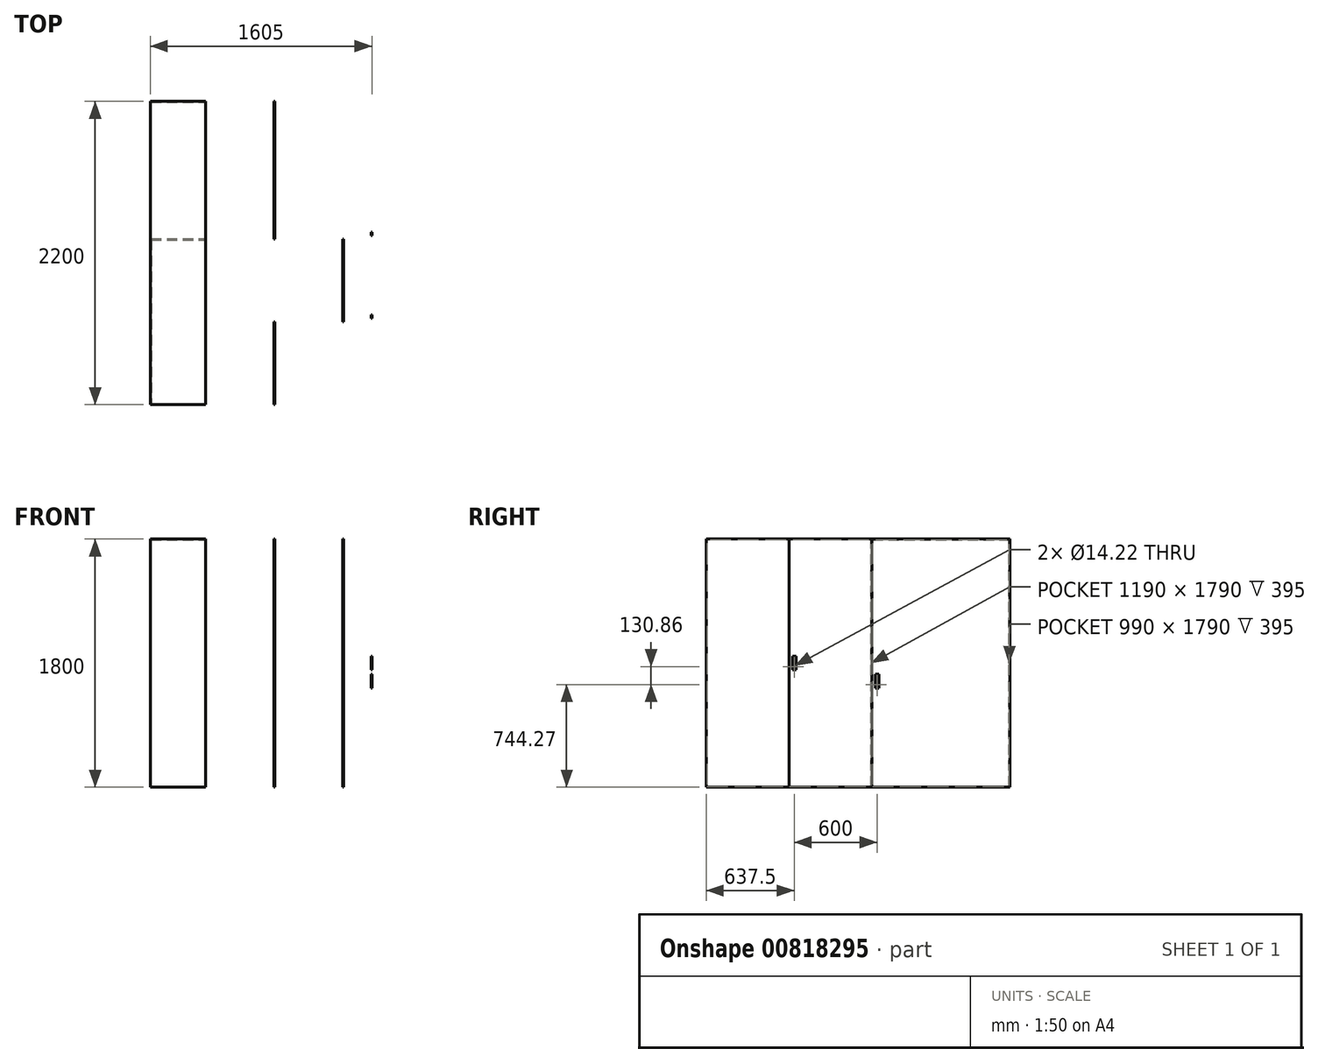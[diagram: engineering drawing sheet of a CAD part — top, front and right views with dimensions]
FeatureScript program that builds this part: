
annotation { "Feature Type Name" : "Feature", "Feature Type Description" : "" }
export const myFeature = defineFeature(function(context is Context, id is Id, definition is map)
    precondition{}
    {
        {
            var Q0;
            Q0=qCreatedBy(makeId("Right.planeOp"),FACE);
            var sketch = newSketch(context, id + "F0", { "sketchPlane" : qUnion([Q0])});
            skLineSegment(sketch, "E0.bottom", {"start": v(0, 0) * mm, "end": v(-1200, 0) * mm});
            skLineSegment(sketch, "E0.top", {"start": v(0, 1800) * mm, "end": v(-1200, 1800) * mm});
            skLineSegment(sketch, "E0.left", {"start": v(0, 0) * mm, "end": v(0, 1800) * mm});
            skLineSegment(sketch, "E0.right", {"start": v(-1200, 0) * mm, "end": v(-1200, 1800) * mm});
            skSolve(sketch);
        }
        {
            var Q0;
            Q0 = qSketchRegion(id + "F0", true);
            extrude(context, id + "F1", {"entities" : qUnion([Q0]), "oppositeDirection" : true, "depth" : 400 * mm, "offsetDistance" : 25 * mm});
        }
        {
            var Q0;
            Q0=qCreatedBy(makeId("Right.planeOp"),FACE);
            var sketch = newSketch(context, id + "F2", { "sketchPlane" : qUnion([Q0])});
            skLineSegment(sketch, "E1.bottom", {"start": v(0, 0) * mm, "end": v(1000, 0) * mm});
            skLineSegment(sketch, "E1.top", {"start": v(0, 1800) * mm, "end": v(1000, 1800) * mm});
            skLineSegment(sketch, "E1.left", {"start": v(0, 0) * mm, "end": v(0, 1800) * mm});
            skLineSegment(sketch, "E1.right", {"start": v(1000, 0) * mm, "end": v(1000, 1800) * mm});
            skSolve(sketch);
        }
        {
            var Q0;
            Q0 = qSketchRegion(id + "F2", true);
            extrude(context, id + "F3", {"entities" : qUnion([Q0]), "oppositeDirection" : true, "depth" : 400 * mm, "offsetDistance" : 25 * mm});
        }
        {
            var Q0;
            Q0=makeQuery(id+"F1.opExtrude","CAP_FACE",FACE,{"disambiguationData":[OSD([sQuery(id+"F0.wireOp",EDGE,"E0.bottom"),sQuery(id+"F0.wireOp",EDGE,"E0.top"),sQuery(id+"F0.wireOp",EDGE,"E0.right"),sQuery(id+"F0.wireOp",EDGE,"E0.left")])],"isStart":true});
            var Q1;
            Q1=makeQuery(id+"F3.opExtrude","CAP_FACE",FACE,{"disambiguationData":[OSD([sQuery(id+"F2.wireOp",EDGE,"E1.bottom"),sQuery(id+"F2.wireOp",EDGE,"E1.top"),sQuery(id+"F2.wireOp",EDGE,"E1.left"),sQuery(id+"F2.wireOp",EDGE,"E1.right")])],"isStart":true});
            shell(context, id + "F4", {"entities" : qUnion([Q0, Q1]), "thickness" : 5 * mm});
        }
        {
            var Q0;
            Q0=makeQuery(id+"F1.opExtrude","SWEPT_BODY",BODY,{"disambiguationData":[OSD([sQuery(id+"F0.wireOp",EDGE,"E0.bottom"),sQuery(id+"F0.wireOp",EDGE,"E0.top"),sQuery(id+"F0.wireOp",EDGE,"E0.right"),sQuery(id+"F0.wireOp",EDGE,"E0.left")])]});
            var Q1;
            Q1=makeQuery(id+"F3.opExtrude","SWEPT_BODY",BODY,{"disambiguationData":[OSD([sQuery(id+"F2.wireOp",EDGE,"E1.bottom"),sQuery(id+"F2.wireOp",EDGE,"E1.top"),sQuery(id+"F2.wireOp",EDGE,"E1.left"),sQuery(id+"F2.wireOp",EDGE,"E1.right")])]});
            booleanBodies(context, id + "F5", {"operationType" : BooleanOperationType.UNION, "tools" : qUnion([Q0, Q1])});
        }
        {
            var Q0;
            Q0=qCreatedBy(makeId("Right.planeOp"),FACE);
            cPlane(context, id + "F6", {"entities" : qUnion([Q0]), "cplaneType" : CPlaneType.OFFSET, "offset" : 500 * mm, "width" : 150 * mm, "height" : 150 * mm});
        }
        {
            var Q0;
            Q0=qCreatedBy(id+"F6.planeOp",FACE);
            var sketch = newSketch(context, id + "F7", { "sketchPlane" : qUnion([Q0])});
            skLineSegment(sketch, "E2.0", {"start": v(1000, 0) * mm, "end": v(1000, 1800) * mm});
            skLineSegment(sketch, "E3.0", {"start": v(-1200, 0) * mm, "end": v(-1200, 1800) * mm});
            skLineSegment(sketch, "E4", {"start": v(1000, 0) * mm, "end": v(0, 0) * mm});
            skLineSegment(sketch, "E5", {"start": v(0, 0) * mm, "end": v(0, 1800) * mm});
            skLineSegment(sketch, "E6", {"start": v(0, 1800) * mm, "end": v(1000, 1800) * mm});
            skLineSegment(sketch, "E7", {"start": v(-1200, 1800) * mm, "end": v(-600, 1800) * mm});
            skLineSegment(sketch, "E8", {"start": v(-600, 1800) * mm, "end": v(-600, 0) * mm});
            skLineSegment(sketch, "E9", {"start": v(-600, 0) * mm, "end": v(-1200, 0) * mm});
            skSolve(sketch);
        }
        {
            var Q0;
            Q0 = qSketchRegion(id + "F7", true);
            extrude(context, id + "F8", {"entities" : qUnion([Q0]), "oppositeDirection" : true, "depth" : 5 * mm, "offsetDistance" : 25 * mm});
        }
        {
            var Q0;
            Q0=qCreatedBy(id+"F6.planeOp",FACE);
            cPlane(context, id + "F9", {"entities" : qUnion([Q0]), "cplaneType" : CPlaneType.OFFSET, "offset" : 500 * mm, "width" : 150 * mm, "height" : 150 * mm});
        }
        {
            var Q0;
            Q0=qCreatedBy(id+"F9.planeOp",FACE);
            var sketch = newSketch(context, id + "F10", { "sketchPlane" : qUnion([Q0])});
            skLineSegment(sketch, "E10.0", {"start": v(-600, 1800) * mm, "end": v(-600, 0) * mm});
            skLineSegment(sketch, "E11.0", {"start": v(0, 0) * mm, "end": v(0, 1800) * mm});
            skLineSegment(sketch, "E12", {"start": v(-600, 1800) * mm, "end": v(0, 1800) * mm});
            skLineSegment(sketch, "E13", {"start": v(-600, 0) * mm, "end": v(0, 0) * mm});
            skSolve(sketch);
        }
        {
            var Q0;
            Q0 = qSketchRegion(id + "F10", true);
            extrude(context, id + "F11", {"entities" : qUnion([Q0]), "oppositeDirection" : true, "depth" : 5 * mm, "offsetDistance" : 25 * mm});
        }
        {
            var Q0;
            Q0=makeQuery(id+"F11.opExtrude","CAP_FACE",FACE,{"disambiguationData":[OSD([sQuery(id+"F10.wireOp",EDGE,"E10.0"),sQuery(id+"F10.wireOp",EDGE,"E11.0"),sQuery(id+"F10.wireOp",EDGE,"E12"),sQuery(id+"F10.wireOp",EDGE,"E13")])],"isStart":true});
            var sketch = newSketch(context, id + "F12", { "sketchPlane" : qUnion([Q0])});
            skLineSegment(sketch, "E14", {"start": v(-575, 0) * mm, "end": v(-575, 850.13) * mm, "construction": true});
            skLineSegment(sketch, "E15.bottom", {"start": v(-575, 850.13) * mm, "end": v(-550, 850.13) * mm});
            skLineSegment(sketch, "E15.top", {"start": v(-575, 950.13) * mm, "end": v(-550, 950.13) * mm});
            skLineSegment(sketch, "E15.left", {"start": v(-575, 850.13) * mm, "end": v(-575, 950.13) * mm});
            skLineSegment(sketch, "E15.right", {"start": v(-550, 850.13) * mm, "end": v(-550, 950.13) * mm});
            skCircle(sketch, "E16", {"center": v(-562.5, 875.13) * mm, "radius": 7.11 * mm});
            skPoint(sketch, "E16.centerSnap0", {"position": v(-562.5, 850.13) * mm});
            skSolve(sketch);
        }
        {
            var Q0;
            Q0 = qSketchRegion(id + "F12", true);
            extrude(context, id + "F13", {"entities" : qUnion([Q0]), "depth" : 5 * mm, "offsetDistance" : 25 * mm});
        }
        {
            var Q0;
            Q0=makeQuery(id+"F11.opExtrude","CAP_FACE",FACE,{"disambiguationData":[OSD([sQuery(id+"F10.wireOp",EDGE,"E10.0"),sQuery(id+"F10.wireOp",EDGE,"E11.0"),sQuery(id+"F10.wireOp",EDGE,"E12"),sQuery(id+"F10.wireOp",EDGE,"E13")])],"isStart":true});
            cPlane(context, id + "F14", {"entities" : qUnion([Q0]), "cplaneType" : CPlaneType.OFFSET, "offset" : 200 * mm, "width" : 150 * mm, "height" : 150 * mm});
        }
        {
            var Q0;
            Q0=qCreatedBy(id+"F14.planeOp",FACE);
            var sketch = newSketch(context, id + "F15", { "sketchPlane" : qUnion([Q0])});
            skLineSegment(sketch, "E17.0.0", {"start": v(-550, 950.13) * mm, "end": v(-575, 950.13) * mm});
            skLineSegment(sketch, "E17.0.1", {"start": v(-575, 950.13) * mm, "end": v(-575, 850.13) * mm});
            skLineSegment(sketch, "E17.0.2", {"start": v(-575, 850.13) * mm, "end": v(-550, 850.13) * mm});
            skLineSegment(sketch, "E17.0.3", {"start": v(-550, 850.13) * mm, "end": v(-550, 950.13) * mm});
            skCircle(sketch, "E18.0", {"center": v(-562.5, 875.13) * mm, "radius": 7.11 * mm});
            skLineSegment(sketch, "E19", {"start": v(25, 0) * mm, "end": v(25, 719.27) * mm, "construction": true});
            skLineSegment(sketch, "E20.0.0", {"start": v(50, 819.27) * mm, "end": v(25, 819.27) * mm});
            skLineSegment(sketch, "E20.0.1", {"start": v(25, 819.27) * mm, "end": v(25, 719.27) * mm});
            skLineSegment(sketch, "E20.0.2", {"start": v(25, 719.27) * mm, "end": v(50, 719.27) * mm});
            skLineSegment(sketch, "E20.0.3", {"start": v(50, 719.27) * mm, "end": v(50, 819.27) * mm});
            skCircle(sketch, "E21.0", {"center": v(37.5, 744.27) * mm, "radius": 7.11 * mm});
            skSolve(sketch);
        }
        {
            var Q0;
            Q0 = qSketchRegion(id + "F15", true);
            extrude(context, id + "F16", {"entities" : qUnion([Q0]), "depth" : 5 * mm, "offsetDistance" : 25 * mm});
        }
        {
            var Q0;
            Q0=makeQuery(id+"F13.opExtrude","SWEPT_BODY",BODY,{"disambiguationData":[OSD([sQuery(id+"F12.wireOp",EDGE,"E15.bottom"),sQuery(id+"F12.wireOp",EDGE,"E15.top"),sQuery(id+"F12.wireOp",EDGE,"E15.left"),sQuery(id+"F12.wireOp",EDGE,"E15.right"),sQuery(id+"F12.wireOp",EDGE,"E16")])]});
            deleteBodies(context, id + "F17", {"entities" : qUnion([Q0])});
        }
    });
